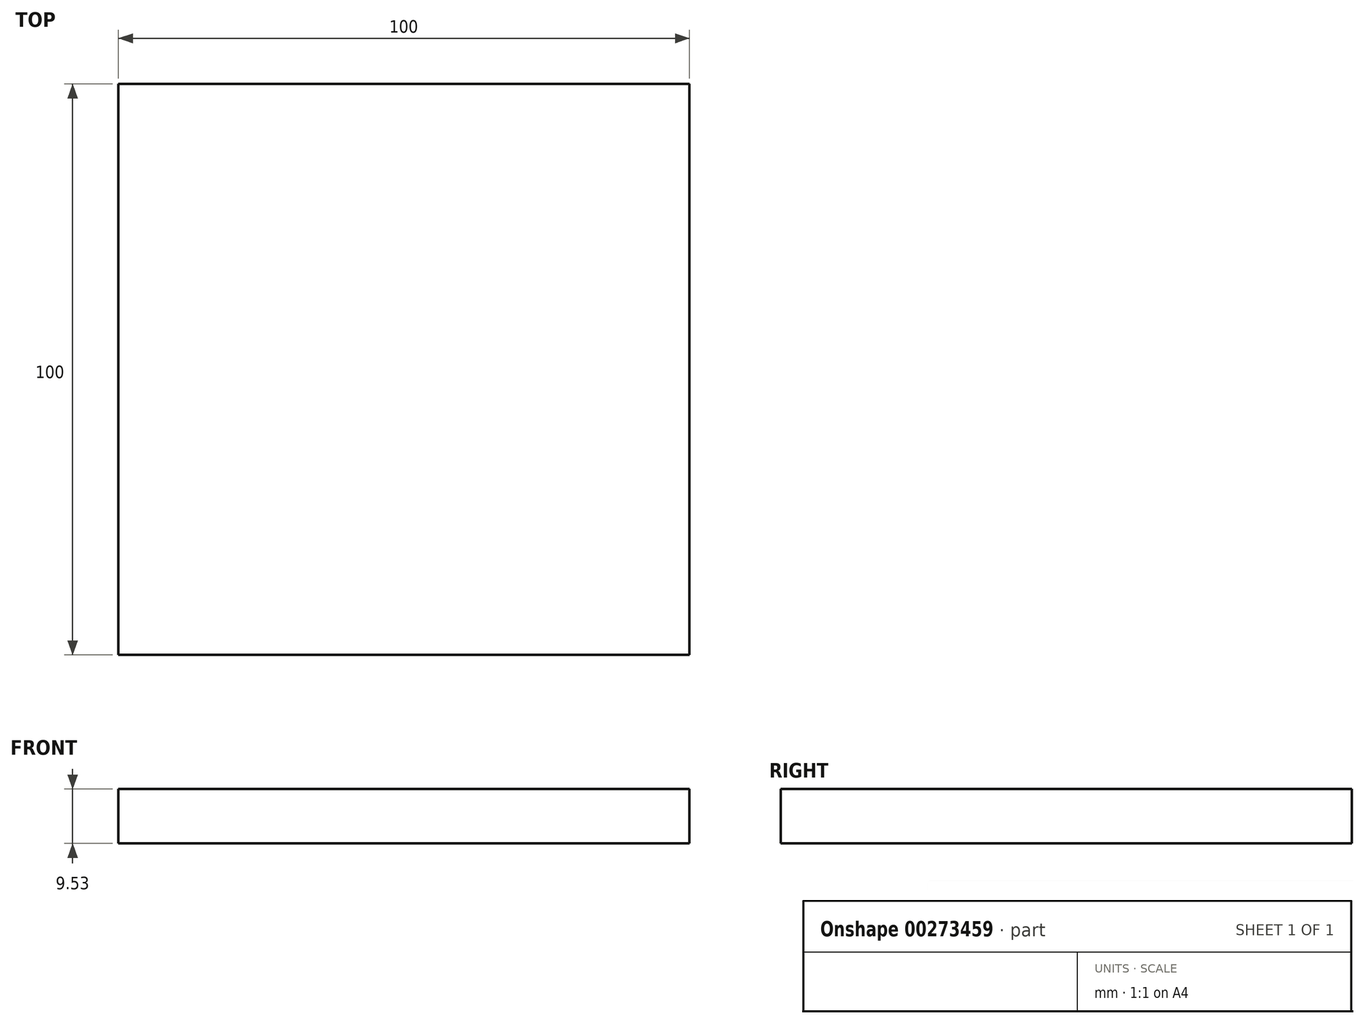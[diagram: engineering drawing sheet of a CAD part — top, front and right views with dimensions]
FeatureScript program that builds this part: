
annotation { "Feature Type Name" : "Feature", "Feature Type Description" : "" }
export const myFeature = defineFeature(function(context is Context, id is Id, definition is map)
    precondition{}
    {
        {
            var Q0;
            Q0=qCreatedBy(makeId("Top.planeOp"),FACE);
            var sketch = newSketch(context, id + "F0", { "sketchPlane" : qUnion([Q0])});
            skLineSegment(sketch, "E0.bottom", {"start": v(2133.6, -2438.4) * mm, "end": v(-2133.6, -2438.4) * mm, "construction": true});
            skLineSegment(sketch, "E0.top", {"start": v(2133.6, 2438.4) * mm, "end": v(-2133.6, 2438.4) * mm, "construction": true});
            skLineSegment(sketch, "E0.left", {"start": v(2133.6, -2438.4) * mm, "end": v(2133.6, 2438.4) * mm, "construction": true});
            skLineSegment(sketch, "E0.right", {"start": v(-2133.6, -2438.4) * mm, "end": v(-2133.6, 2438.4) * mm, "construction": true});
            skPoint(sketch, "E0.middle", {"position": v(0, 0) * mm});
            skLineSegment(sketch, "E1.bottom", {"start": v(-1981.2, 2286) * mm, "end": v(-1066.8, 2286) * mm, "construction": true});
            skLineSegment(sketch, "E1.top", {"start": v(-1981.2, -1371.6) * mm, "end": v(-1066.8, -1371.6) * mm, "construction": true});
            skLineSegment(sketch, "E1.left", {"start": v(-1981.2, 2286) * mm, "end": v(-1981.2, -1371.6) * mm, "construction": true});
            skLineSegment(sketch, "E1.right", {"start": v(-1066.8, 2286) * mm, "end": v(-1066.8, -1371.6) * mm, "construction": true});
            skLineSegment(sketch, "E2", {"start": v(-1981.2, 1371.6) * mm, "end": v(-1066.8, 1371.6) * mm, "construction": true});
            skLineSegment(sketch, "E3", {"start": v(-1066.8, -457.2) * mm, "end": v(-1981.2, -457.2) * mm, "construction": true});
            skLineSegment(sketch, "E4", {"start": v(0, 0) * mm, "end": v(0, 2769.23) * mm, "construction": true});
            skLineSegment(sketch, "E5.MirrorCS", {"start": v(1981.2, -1371.6) * mm, "end": v(1066.8, -1371.6) * mm, "construction": true});
            skLineSegment(sketch, "E6.MirrorCS", {"start": v(1066.8, -457.2) * mm, "end": v(1981.2, -457.2) * mm, "construction": true});
            skLineSegment(sketch, "E7.MirrorCS", {"start": v(1981.2, 1371.6) * mm, "end": v(1066.8, 1371.6) * mm, "construction": true});
            skLineSegment(sketch, "E8.MirrorCS", {"start": v(1981.2, 2286) * mm, "end": v(1981.2, -1371.6) * mm, "construction": true});
            skLineSegment(sketch, "E9.MirrorCS", {"start": v(1981.2, 2286) * mm, "end": v(1066.8, 2286) * mm, "construction": true});
            skLineSegment(sketch, "E10.MirrorCS", {"start": v(1066.8, 2286) * mm, "end": v(1066.8, -1371.6) * mm, "construction": true});
            skLineSegment(sketch, "E11", {"start": v(-1981.2, 2286) * mm, "end": v(-1066.8, 1371.6) * mm, "construction": true});
            skPoint(sketch, "E12", {"position": v(-1524, 1828.8) * mm});
            skLineSegment(sketch, "E13", {"start": v(-1981.2, -457.2) * mm, "end": v(-1066.8, -1371.6) * mm, "construction": true});
            skPoint(sketch, "E14", {"position": v(-1524, -914.4) * mm});
            skPoint(sketch, "E15.MirrorP", {"position": v(1524, 1828.8) * mm});
            skPoint(sketch, "E16.MirrorP", {"position": v(1524, -914.4) * mm});
            skLineSegment(sketch, "E17", {"start": v(-1981.2, 457.2) * mm, "end": v(-1066.8, 457.2) * mm, "construction": true});
            skLineSegment(sketch, "E18", {"start": v(-1981.2, 1371.6) * mm, "end": v(-1066.8, 457.2) * mm, "construction": true});
            skLineSegment(sketch, "E19", {"start": v(-1981.2, 457.2) * mm, "end": v(-1066.8, -457.2) * mm, "construction": true});
            skPoint(sketch, "E20", {"position": v(-1524, 914.4) * mm});
            skPoint(sketch, "E21", {"position": v(-1524, 0) * mm});
            skPoint(sketch, "E22.MirrorP", {"position": v(1524, 914.4) * mm});
            skPoint(sketch, "E23.MirrorP", {"position": v(1524, 0) * mm});
            skLineSegment(sketch, "E24.bottom", {"start": v(-457.2, 2286) * mm, "end": v(457.2, 2286) * mm, "construction": true});
            skLineSegment(sketch, "E24.left", {"start": v(-457.2, 2286) * mm, "end": v(-457.2, -1371.6) * mm, "construction": true});
            skLineSegment(sketch, "E24.right", {"start": v(457.2, 2286) * mm, "end": v(457.2, -1371.6) * mm, "construction": true});
            skLineSegment(sketch, "E25", {"start": v(457.2, -1371.6) * mm, "end": v(-457.2, -1371.6) * mm, "construction": true});
            skLineSegment(sketch, "E26", {"start": v(-457.2, 1371.6) * mm, "end": v(457.2, 1371.6) * mm, "construction": true});
            skLineSegment(sketch, "E27", {"start": v(-457.2, 457.2) * mm, "end": v(457.2, 457.2) * mm, "construction": true});
            skLineSegment(sketch, "E28", {"start": v(-457.2, -457.2) * mm, "end": v(457.2, -457.2) * mm, "construction": true});
            skLineSegment(sketch, "E29.MirrorCS", {"start": v(1981.2, 457.2) * mm, "end": v(1066.8, 457.2) * mm, "construction": true});
            skSolve(sketch);
        }
        {
            var Q0;
            Q0=qCreatedBy(makeId("Top.planeOp"),FACE);
            cPlane(context, id + "F1", {"entities" : qUnion([Q0]), "cplaneType" : CPlaneType.OFFSET, "offset" : 1219.2 * mm, "width" : 152.4 * mm, "height" : 152.4 * mm});
        }
        {
            var Q0;
            Q0=qCreatedBy(id+"F1.planeOp",FACE);
            var sketch = newSketch(context, id + "F2", { "sketchPlane" : qUnion([Q0])});
            skLineSegment(sketch, "E30.0", {"start": v(-1066.8, 2286) * mm, "end": v(-1066.8, -1371.6) * mm, "construction": true});
            skLineSegment(sketch, "E31.0", {"start": v(-1981.2, 2286) * mm, "end": v(-1066.8, 2286) * mm, "construction": true});
            skLineSegment(sketch, "E32.0", {"start": v(-1981.2, 2286) * mm, "end": v(-1066.8, 1371.6) * mm, "construction": true});
            skLineSegment(sketch, "E33.0", {"start": v(-1981.2, 2286) * mm, "end": v(-1981.2, -1371.6) * mm, "construction": true});
            skLineSegment(sketch, "E34.0", {"start": v(-1981.2, 1371.6) * mm, "end": v(-1066.8, 1371.6) * mm, "construction": true});
            skLineSegment(sketch, "E35.0", {"start": v(-1981.2, 1371.6) * mm, "end": v(-1066.8, 457.2) * mm, "construction": true});
            skLineSegment(sketch, "E36.0", {"start": v(-1981.2, 457.2) * mm, "end": v(-1066.8, 457.2) * mm, "construction": true});
            skLineSegment(sketch, "E37.0", {"start": v(-1981.2, 457.2) * mm, "end": v(-1066.8, -457.2) * mm, "construction": true});
            skLineSegment(sketch, "E38.0", {"start": v(-1066.8, -457.2) * mm, "end": v(-1981.2, -457.2) * mm, "construction": true});
            skLineSegment(sketch, "E39.0", {"start": v(-1981.2, -457.2) * mm, "end": v(-1066.8, -1371.6) * mm, "construction": true});
            skLineSegment(sketch, "E40.0", {"start": v(-1981.2, -1371.6) * mm, "end": v(-1066.8, -1371.6) * mm, "construction": true});
            skLineSegment(sketch, "E41.0", {"start": v(-457.2, 2286) * mm, "end": v(457.2, 2286) * mm, "construction": true});
            skLineSegment(sketch, "E42.0", {"start": v(-457.2, 2286) * mm, "end": v(-457.2, -1371.6) * mm, "construction": true});
            skLineSegment(sketch, "E43.0", {"start": v(-457.2, 1371.6) * mm, "end": v(457.2, 1371.6) * mm, "construction": true});
            skLineSegment(sketch, "E44.0", {"start": v(-457.2, 457.2) * mm, "end": v(457.2, 457.2) * mm, "construction": true});
            skLineSegment(sketch, "E45.0", {"start": v(-457.2, -457.2) * mm, "end": v(457.2, -457.2) * mm, "construction": true});
            skLineSegment(sketch, "E46.0", {"start": v(457.2, -1371.6) * mm, "end": v(-457.2, -1371.6) * mm, "construction": true});
            skLineSegment(sketch, "E47.0", {"start": v(457.2, 2286) * mm, "end": v(457.2, -1371.6) * mm, "construction": true});
            skLineSegment(sketch, "E48.0", {"start": v(1066.8, 2286) * mm, "end": v(1066.8, -1371.6) * mm, "construction": true});
            skLineSegment(sketch, "E49.0", {"start": v(1981.2, 457.2) * mm, "end": v(1066.8, 457.2) * mm, "construction": true});
            skLineSegment(sketch, "E50.0", {"start": v(1066.8, -457.2) * mm, "end": v(1981.2, -457.2) * mm, "construction": true});
            skLineSegment(sketch, "E51.0", {"start": v(1981.2, -1371.6) * mm, "end": v(1066.8, -1371.6) * mm, "construction": true});
            skLineSegment(sketch, "E52.0", {"start": v(1981.2, 2286) * mm, "end": v(1981.2, -1371.6) * mm, "construction": true});
            skLineSegment(sketch, "E53.0", {"start": v(1981.2, 2286) * mm, "end": v(1066.8, 2286) * mm, "construction": true});
            skLineSegment(sketch, "E54.0", {"start": v(1981.2, 1371.6) * mm, "end": v(1066.8, 1371.6) * mm, "construction": true});
            skSolve(sketch);
        }
        {
            var Q0;
            Q0=qCreatedBy(id+"F1.planeOp",FACE);
            var sketch = newSketch(context, id + "F3", { "sketchPlane" : qUnion([Q0])});
            skPoint(sketch, "E55", {"position": v(-1524, 1828.8) * mm});
            skLineSegment(sketch, "E56", {"start": v(-1524, 2436.04) * mm, "end": v(-1524, 1828.8) * mm, "construction": true});
            skLineSegment(sketch, "E57", {"start": v(-1524, 1828.8) * mm, "end": v(-928.36, 1828.8) * mm, "construction": true});
            skLineSegment(sketch, "E58.right", {"start": v(-1878.8, 2083.6) * mm, "end": v(-1878.8, 2183.6) * mm});
            skLineSegment(sketch, "E59.bottom", {"start": v(-1169.2, 1778.8) * mm, "end": v(-1878.8, 1778.8) * mm, "construction": true});
            skLineSegment(sketch, "E59.top", {"start": v(-1169.2, 1878.8) * mm, "end": v(-1878.8, 1878.8) * mm, "construction": true});
            skLineSegment(sketch, "E59.left", {"start": v(-1169.2, 1778.8) * mm, "end": v(-1169.2, 1878.8) * mm, "construction": true});
            skLineSegment(sketch, "E59.right", {"start": v(-1878.8, 1778.8) * mm, "end": v(-1878.8, 1878.8) * mm, "construction": true});
            skLineSegment(sketch, "E60.MirrorCS", {"start": v(-1169.2, 1574) * mm, "end": v(-1878.8, 1574) * mm, "construction": true});
            skLineSegment(sketch, "E61.MirrorCS", {"start": v(-1169.2, 1474) * mm, "end": v(-1878.8, 1474) * mm, "construction": true});
            skLineSegment(sketch, "E62.MirrorCS", {"start": v(-1169.2, 1574) * mm, "end": v(-1169.2, 1474) * mm, "construction": true});
            skLineSegment(sketch, "E63.MirrorCS", {"start": v(-1878.8, 1574) * mm, "end": v(-1878.8, 1474) * mm, "construction": true});
            skPoint(sketch, "E64", {"position": v(-1169.2, 2133.6) * mm});
            skPoint(sketch, "E65", {"position": v(-1625.6, 2133.6) * mm});
            skPoint(sketch, "E66", {"position": v(-1828.8, 2133.6) * mm});
            skLineSegment(sketch, "E67", {"start": v(-1878.8, 2133.6) * mm, "end": v(-1169.2, 2133.6) * mm, "construction": true});
            skPoint(sketch, "E68.MirrorP", {"position": v(-1219.2, 2133.6) * mm});
            skPoint(sketch, "E69.MirrorP", {"position": v(-1422.4, 2133.6) * mm});
            skLineSegment(sketch, "E70", {"start": v(-1778.8, 2183.6) * mm, "end": v(-1778.8, 2083.6) * mm});
            skLineSegment(sketch, "E71.trimOffspring", {"start": v(-1778.8, 2183.6) * mm, "end": v(-1878.8, 2183.6) * mm});
            skLineSegment(sketch, "E72.trimOffspring", {"start": v(-1778.8, 2083.6) * mm, "end": v(-1878.8, 2083.6) * mm});
            skSolve(sketch);
        }
        {
            var Q0;
            Q0 = qSketchRegion(id + "F3", true);
            extrude(context, id + "F4", {"entities" : qUnion([Q0]), "depth" : 9.52 * mm});
        }
    });
